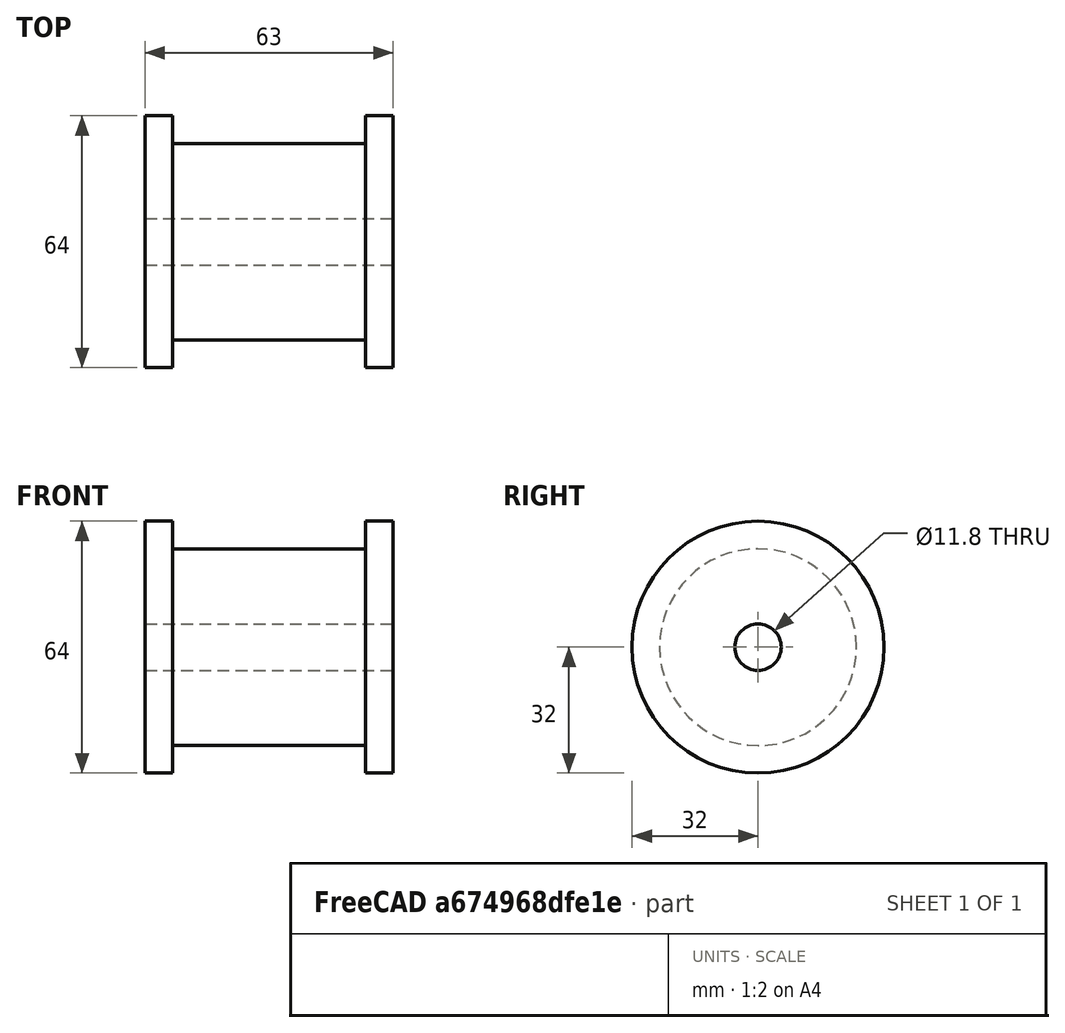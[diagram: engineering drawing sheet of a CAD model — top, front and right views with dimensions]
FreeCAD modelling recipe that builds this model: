
FCSTD DOCUMENT  (FreeCAD 0.20R28730 (Git))
Label: Spool Dummy
License: All rights reserved
LicenseURL: http://en.wikipedia.org/wiki/All_rights_reserved
objects: Sketcher::SketchObject×1, PartDesign::Revolution×1, PartDesign::CoordinateSystem×1, PartDesign::Body×1
note: 5 computed .brp shape members not serialized (recipe doc carries the construction recipe); baked Part::Feature solids carry a one-line shape summary decoded from their .brp

FEATURE [Sketcher::SketchObject] Sketch
  FullyConstrained = true
  MapMode = 5
  Placement = pos=(0,0,0) rot=(1,0,0;1.5708rad)
  Support = -> [XZ_Plane]
  sketch-geometry (10):
    g0: LineSegment StartX=31.5 StartY=5.9 StartZ=0 EndX=31.5 EndY=32 EndZ=0
    g1: LineSegment StartX=31.5 StartY=32 StartZ=0 EndX=-31.5 EndY=32 EndZ=0
    g2: LineSegment StartX=-31.5 StartY=32 StartZ=0 EndX=-31.5 EndY=5.9 EndZ=0
    g3: LineSegment StartX=-31.5 StartY=5.9 StartZ=0 EndX=31.5 EndY=5.9 EndZ=0
    g4: GeomPoint X=0 Y=18.95 Z=0
    g5: LineSegment StartX=-24.5 StartY=32 StartZ=0 EndX=-24.5 EndY=25 EndZ=0
    g6: LineSegment StartX=-24.5 StartY=25 StartZ=0 EndX=24.5 EndY=25 EndZ=0
    g7: LineSegment StartX=24.5 StartY=25 StartZ=0 EndX=24.5 EndY=32 EndZ=0
    g8: LineSegment StartX=-31.5 StartY=32 StartZ=0 EndX=-24.5 EndY=32 EndZ=0
    g9: LineSegment StartX=24.5 StartY=32 StartZ=0 EndX=31.5 EndY=32 EndZ=0
  constraints (27):
    c: Coincident(g0,g1)
    c: Coincident(g1,g2)
    c: Coincident(g2,g3)
    c: Coincident(g3,g0)
    c: Horizontal(g1)
    c: Horizontal(g3)
    c: Vertical(g0)
    c: Vertical(g2)
    c: Symmetric(g1,g0,g4)
    c: PointOnObject(g4,g-2)
    c: PointOnObject(g5,g1)
    c: Vertical(g5)
    c: Coincident(g5,g6)
    c: Horizontal(g6)
    c: Coincident(g6,g7)
    c: PointOnObject(g7,g1)
    c: Vertical(g7)
    c: Coincident(g8,g2)
    c: Coincident(g8,g5)
    c: Coincident(g9,g7)
    c: Coincident(g9,g0)
    c: Equal(g8,g9)
    c: DistanceX(g3,g3) = 63
    c: DistanceX(g8,g8) = 7
    c: DistanceY(g-1,g2) = 5.9
    c: DistanceY(g-1,g5) = 25
    c: DistanceY(g-1,g2) = 32
FEATURE [PartDesign::Revolution] Revolution
  Angle = 360
  Axis = (1,0,0)
  Base = (0,0,0)
  Placement = pos=(0,0,0) rot=(1,0,0;1.5708rad)
  Profile = -> Sketch
  ReferenceAxis = -> X_Axis
FEATURE [PartDesign::CoordinateSystem] LCS_1  label="LCS_Spool_Dummy"
  AttacherType = Attacher::AttachEngine3D
  MapMode = 11
  Placement = pos=(31.5,0,0) rot=(0.57735,-0.57735,0.57735;4.18879rad)
  Support = -> [Revolution]
FEATURE [PartDesign::Body] Body  label="Spool_Dummy"
  Group = -> [Sketch,Revolution,LCS_1]
  Origin = -> Origin
  Tip = -> Revolution
